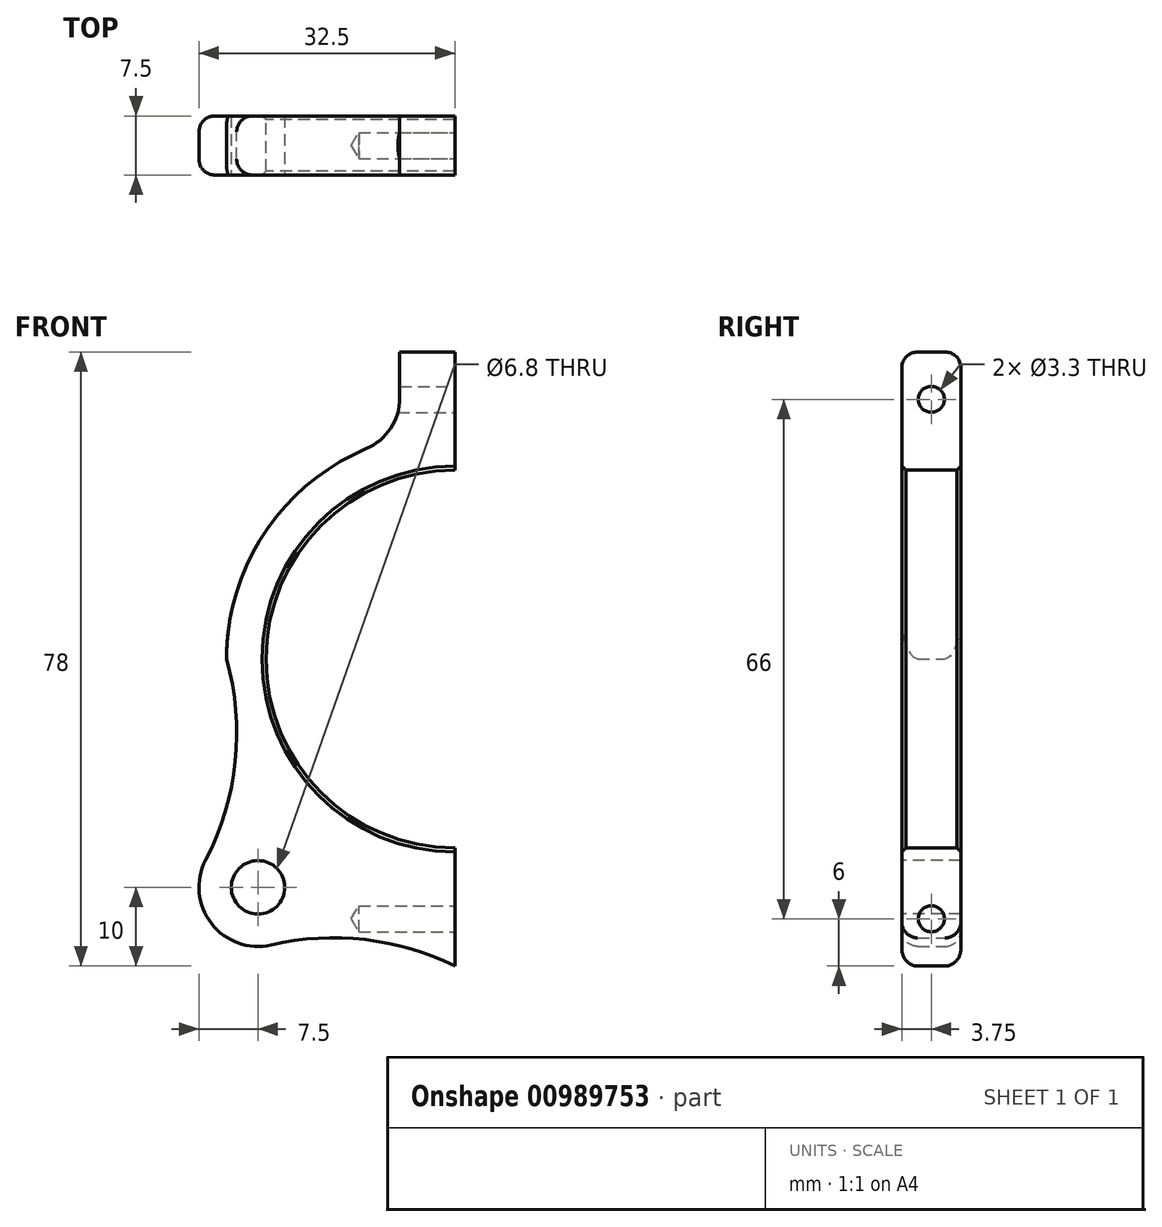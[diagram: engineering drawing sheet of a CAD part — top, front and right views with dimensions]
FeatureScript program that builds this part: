
annotation { "Feature Type Name" : "Feature", "Feature Type Description" : "" }
export const myFeature = defineFeature(function(context is Context, id is Id, definition is map)
    precondition{}
    {
        {
            var Q0;
            Q0=qCreatedBy(makeId("Front.planeOp"),FACE);
            var sketch = newSketch(context, id + "F0", { "sketchPlane" : qUnion([Q0])});
            skArc(sketch, "E0", {"start": v(0, 24) * mm, "mid": v(-24, 0) * mm, "end": v(0, -24) * mm});
            skArc(sketch, "E1", {"start": v(-7, 28.14) * mm, "mid": v(-22.85, 17.86) * mm, "end": v(-29, 0) * mm});
            skLineSegment(sketch, "E2", {"start": v(0, 24) * mm, "end": v(0, 39) * mm});
            skLineSegment(sketch, "E3", {"start": v(0, 39) * mm, "end": v(-7, 39) * mm});
            skLineSegment(sketch, "E4", {"start": v(-7, 39) * mm, "end": v(-7, 28.14) * mm});
            skLineSegment(sketch, "E5", {"start": v(0, -24) * mm, "end": v(0, -39) * mm});
            skLineSegment(sketch, "E6.trimOffspring", {"start": v(-14.06, -25.36) * mm, "end": v(-14.06, -25.36) * mm});
            skArc(sketch, "E7", {"start": v(-31.66, -25.54) * mm, "mid": v(-30.93, -33.6) * mm, "end": v(-23.31, -36.3) * mm});
            skArc(sketch, "E8", {"start": v(-31.66, -25.54) * mm, "mid": v(-27.9, -13.02) * mm, "end": v(-29, 0) * mm});
            skArc(sketch, "E9", {"start": v(0, -39) * mm, "mid": v(-11.42, -35.64) * mm, "end": v(-23.31, -36.3) * mm});
            skSolve(sketch);
        }
        {
            var Q0;
            Q0=makeQuery(id+"F0.imprint","IMPRINT",FACE,{"disambiguationData":[TD([[makeQuery(id+"F0.imprint","IMPRINT",EDGE,{"derivedFrom":sQuery(id+"F0.wireOp",EDGE,"E0")}),-1.0]])]});
            extrude(context, id + "F1", {"entities" : qUnion([Q0]), "depth" : 7.5 * mm, "offsetDistance" : 25 * mm, "symmetric" : true});
        }
        {
            var Q0;
            Q0=makeQuery(id+"F1.opExtrude","SWEPT_FACE",FACE,{"disambiguationData":[OSD([sQuery(id+"F0.wireOp",EDGE,"E2")])]});
            var sketch = newSketch(context, id + "F2", { "sketchPlane" : qUnion([Q0])});
            skPoint(sketch, "E10", {"position": v(0, 33) * mm});
            skPoint(sketch, "E11", {"position": v(0, -33) * mm});
            skSolve(sketch);
        }
        {
            var Q0;
            Q0=sQuery(id+"F2.wireOp",VERTEX,"E10");
            var Q1;
            Q1=sQuery(id+"F2.wireOp",VERTEX,"E11");
            var Q2;
            Q2=makeQuery(id+"F1.opExtrude","SWEPT_BODY",BODY,{"disambiguationData":[OSD([sQuery(id+"F0.wireOp",EDGE,"E0"),sQuery(id+"F0.wireOp",EDGE,"E1"),sQuery(id+"F0.wireOp",EDGE,"E2"),sQuery(id+"F0.wireOp",EDGE,"E3"),sQuery(id+"F0.wireOp",EDGE,"E4"),sQuery(id+"F0.wireOp",EDGE,"E5"),sQuery(id+"F0.wireOp",EDGE,"1F1w9NIG-NumR-vg71-TfjA-OamJ2fLqCWXM"),sQuery(id+"F0.wireOp",EDGE,"b2wtoqGv-eT8S-yigE-bfgF-v8djrpwRySl6")])]});
            hole(context, id + "F3", {"style" : HoleStyle.SIMPLE, "endStyle" : HoleEndStyle.BLIND, "standardTappedOrClearance" : lookupTablePath({ "standard" : "ISO", "engagement" : "75%", "pitch" : "0.7 mm", "size" : "M4", "type" : "Tapped" }), "standardBlindInLast" : lookupTablePath({ "standard" : "ISO", "fit" : "Normal", "engagement" : "75%", "pitch" : "0.7 mm", "size" : "M4", "type" : "Clearance & tapped" }), "holeDiameter" : 3.3 * mm, "majorDiameter" : 4 * mm, "showTappedDepth" : true, "holeDepth" : 12.2 * mm, "tappedDepth" : 10.1 * mm, "tapClearance" : 3, "locations" : qUnion([Q0, Q1]), "scope" : qUnion([Q2])});
        }
        {
            var Q0;
            Q0=makeQuery(id+"F1.opExtrude","CAP_EDGE",EDGE,{"disambiguationData":[OSD([sQuery(id+"F0.wireOp",EDGE,"E3")])],"isStart":true});
            var Q1;
            Q1=makeQuery(id+"F1.opExtrude","CAP_EDGE",EDGE,{"disambiguationData":[OSD([sQuery(id+"F0.wireOp",EDGE,"E3")])],"isStart":false});
            var Q2;
            Q2=makeQuery(id+"F1.opExtrude","CAP_EDGE",EDGE,{"disambiguationData":[OSD([sQuery(id+"F0.wireOp",EDGE,"1F1w9NIG-NumR-vg71-TfjA-OamJ2fLqCWXM")])],"isStart":false});
            var Q3;
            Q3=makeQuery(id+"F1.opExtrude","CAP_EDGE",EDGE,{"disambiguationData":[OSD([sQuery(id+"F0.wireOp",EDGE,"1F1w9NIG-NumR-vg71-TfjA-OamJ2fLqCWXM")])],"isStart":true});
            var Q4;
            Q4=makeQuery(id+"F1.opExtrude","CAP_EDGE",EDGE,{"disambiguationData":[OSD([sQuery(id+"F0.wireOp",EDGE,"E9")])],"isStart":true});
            var Q5;
            Q5=makeQuery(id+"F1.opExtrude","CAP_EDGE",EDGE,{"disambiguationData":[OSD([sQuery(id+"F0.wireOp",EDGE,"E9")])],"isStart":false});
            fillet(context, id + "F4", {"entities" : qUnion([Q0, Q1, Q2, Q3, Q4, Q5]), "radius" : 2 * mm, "tangentPropagation" : true, "allowEdgeOverflow" : false});
        }
        {
            var Q0;
            Q0=makeQuery(id+"F1.opExtrude","SWEPT_EDGE",EDGE,{"disambiguationData":[OSD([sQuery(id+"F0.wireOp",EDGE,"E1"),sQuery(id+"F0.wireOp",EDGE,"E4")])]});
            var Q1;
            Q1=makeQuery(id+"F1.opExtrude","SWEPT_EDGE",EDGE,{"disambiguationData":[OSD([sQuery(id+"F0.wireOp",EDGE,"b2wtoqGv-eT8S-yigE-bfgF-v8djrpwRySl6"),sQuery(id+"F0.wireOp",EDGE,"E6.trimOffspring")])]});
            fillet(context, id + "F5", {"entities" : qUnion([Q0, Q1]), "radius" : 7 * mm, "tangentPropagation" : true, "allowEdgeOverflow" : false});
        }
        {
            var Q0;
            Q0=makeQuery(id+"F1.opExtrude","CAP_EDGE",EDGE,{"disambiguationData":[OSD([sQuery(id+"F0.wireOp",EDGE,"E0")])],"isStart":true});
            var Q1;
            Q1=makeQuery(id+"F1.opExtrude","CAP_EDGE",EDGE,{"disambiguationData":[OSD([sQuery(id+"F0.wireOp",EDGE,"E0")])],"isStart":false});
            chamfer(context, id + "F6", {"entities" : qUnion([Q0, Q1]), "width" : 0.5 * mm, "tangentPropagation" : true});
        }
        {
            var Q0;
            Q0=makeQuery(id+"F1.opExtrude","CAP_FACE",FACE,{"disambiguationData":[OSD([sQuery(id+"F0.wireOp",EDGE,"E0"),sQuery(id+"F0.wireOp",EDGE,"E1"),sQuery(id+"F0.wireOp",EDGE,"E2"),sQuery(id+"F0.wireOp",EDGE,"E3"),sQuery(id+"F0.wireOp",EDGE,"E4"),sQuery(id+"F0.wireOp",EDGE,"E5"),sQuery(id+"F0.wireOp",EDGE,"1F1w9NIG-NumR-vg71-TfjA-OamJ2fLqCWXM"),sQuery(id+"F0.wireOp",EDGE,"b2wtoqGv-eT8S-yigE-bfgF-v8djrpwRySl6"),sQuery(id+"F0.wireOp",EDGE,"yK8s0g3W-U7XJ-ORbv-GEI7-T3XzLuHcodY9"),sQuery(id+"F0.wireOp",EDGE,"BUXcghrY-cne4-y3bH-A95m-0iBplFJHcpwy"),sQuery(id+"F0.wireOp",EDGE,"xXkgP4X3-q2zG-kYfN-1DFS-QFpcPexJxHps"),sQuery(id+"F0.wireOp",EDGE,"BXGdM62L-ZtW7-lXHA-5lVo-wDGAsPwAjw5w"),sQuery(id+"F0.wireOp",EDGE,"E6.trimOffspring"),sQuery(id+"F0.wireOp",EDGE,"S8mInYIJ-SRYa-DYCc-F79q-CzpKqlkJmKCX")])],"isStart":false});
            var sketch = newSketch(context, id + "F7", { "sketchPlane" : qUnion([Q0])});
            skPoint(sketch, "E12", {"position": v(-25, -29) * mm});
            skSolve(sketch);
        }
        {
            var Q0;
            Q0=sQuery(id+"F7.wireOp",VERTEX,"E12");
            var Q1;
            Q1=sQuery(id+"F7.wireOp",VERTEX,"57d24044-d913-4d64-b2a4-86b3e8844ea7");
            var Q2;
            Q2=makeQuery(id+"F1.opExtrude","SWEPT_BODY",BODY,{"disambiguationData":[OSD([sQuery(id+"F0.wireOp",EDGE,"E0"),sQuery(id+"F0.wireOp",EDGE,"E1"),sQuery(id+"F0.wireOp",EDGE,"E2"),sQuery(id+"F0.wireOp",EDGE,"E3"),sQuery(id+"F0.wireOp",EDGE,"E4"),sQuery(id+"F0.wireOp",EDGE,"E5"),sQuery(id+"F0.wireOp",EDGE,"1F1w9NIG-NumR-vg71-TfjA-OamJ2fLqCWXM"),sQuery(id+"F0.wireOp",EDGE,"b2wtoqGv-eT8S-yigE-bfgF-v8djrpwRySl6"),sQuery(id+"F0.wireOp",EDGE,"yK8s0g3W-U7XJ-ORbv-GEI7-T3XzLuHcodY9"),sQuery(id+"F0.wireOp",EDGE,"BUXcghrY-cne4-y3bH-A95m-0iBplFJHcpwy"),sQuery(id+"F0.wireOp",EDGE,"xXkgP4X3-q2zG-kYfN-1DFS-QFpcPexJxHps"),sQuery(id+"F0.wireOp",EDGE,"BXGdM62L-ZtW7-lXHA-5lVo-wDGAsPwAjw5w"),sQuery(id+"F0.wireOp",EDGE,"E6.trimOffspring"),sQuery(id+"F0.wireOp",EDGE,"S8mInYIJ-SRYa-DYCc-F79q-CzpKqlkJmKCX")])]});
            hole(context, id + "F8", {"style" : HoleStyle.SIMPLE, "endStyle" : HoleEndStyle.THROUGH, "standardTappedOrClearance" : lookupTablePath({ "standard" : "ISO", "engagement" : "75%", "pitch" : "1.25 mm", "size" : "M8", "type" : "Tapped" }), "standardBlindInLast" : lookupTablePath({ "standard" : "ISO", "fit" : "Normal", "engagement" : "75%", "pitch" : "1.25 mm", "size" : "M8", "type" : "Clearance & tapped" }), "holeDiameter" : 6.8 * mm, "majorDiameter" : 8 * mm, "showTappedDepth" : true, "isTappedThrough" : true, "tappedDepth" : 1 * mm, "tapClearance" : 3, "locations" : qUnion([Q0, Q1]), "scope" : qUnion([Q2])});
        }
    });
